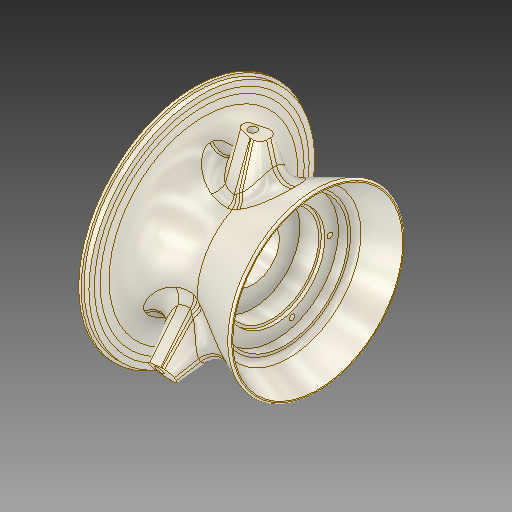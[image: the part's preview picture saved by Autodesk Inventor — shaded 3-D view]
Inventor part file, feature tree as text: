
AUTODESK INVENTOR PART (.ipt)
format: ipt  version: 2019 (Build 230136000, 136)  size: 813,056 bytes
history: native  units: mm
features: sketch x6, fillet x3, extrude x3, hole x2, pattern_circular x2, revolve x1, plane x1, projected_geometry x1
ambient origin geometry x8: Origin, YZ Plane, XZ Plane, XY Plane, X Axis, Y Axis, Z Axis, Center Point
bodies: Solid1 (feature_tree)
feature tree (19):
  revolve  "Revolution1"  [1 undecoded]
  fillet  "Fillet1"  Radius=29.84513mm
  plane  "Work Plane1"
  extrude  "Extrusion1"  Depth=24.0mm
  fillet  "Fillet2"  Radius=20.0mm
  hole  "Hole1"  [1 undecoded]
  pattern_circular  "Circular Pattern1"  [2 undecoded]
  hole  "Hole2"  [1 undecoded]
  pattern_circular  "Circular Pattern2"  [2 undecoded]
  extrude  "Extrusion2"  Depth=1.0mm
  extrude  "Extrusion3"  Depth=1.0mm
  fillet  "Fillet3"  Radius=2.9mm
  sketch  "Sketch1"  dims[d21=4.8mm d22=66.0mm d23=29.84513mm]
  sketch  "Sketch2"  dims[d25=37.35mm d28=24.0mm d29=20.0mm]
  sketch  "Sketch3"  dims[d31=75.0deg d32=2.0mm]
  sketch  "Sketch4"  dims[d35=18.5mm]
  sketch  "Sketch5"  dims[d43=15.5mm]
  sketch  "Sketch6"  dims[d44=27.5mm d46=13.0mm d47=5.6mm d50=37.0mm d51=26.0mm d52=22.0mm d56=2.9mm d57=1.6mm d58=1.0mm d60=3.6mm d61=2.0mm d62=90.0deg d63=4.0mm d64=63.0mm d65=10.0mm d66=2.722714mm d67=28.0mm d68=15.0mm d69=3.8mm d70=2.0mm d71=1.6mm d72=5.5mm d73=5.0mm d74=10.0mm d75=2.792527mm d76=8.0mm d77=5.0mm d78=6.0mm d79=4.0mm d80=2.0mm d81=90.0deg d82=15.0mm d83=0.0mm d84=30.0mm d85=360.0deg d87=32.0mm d88=3.22mm d89=6.0mm d90=4.0mm d91=2.0mm d92=90.0deg d93=10.2mm d94=0.0mm d95=50.0mm d96=360.0deg d98=30.0mm d99=58.0mm d100=2.0mm d101=0.0mm d102=0.5mm d103=0.0mm d104=67.0mm d105=1.0mm]
  projected_geometry  "Projected Loop1"
note: 7 required parameter values undecoded (feature->parameter linkage not recoverable at this tier; creation-order binding heuristic only, values carry confidence <= 0.55)